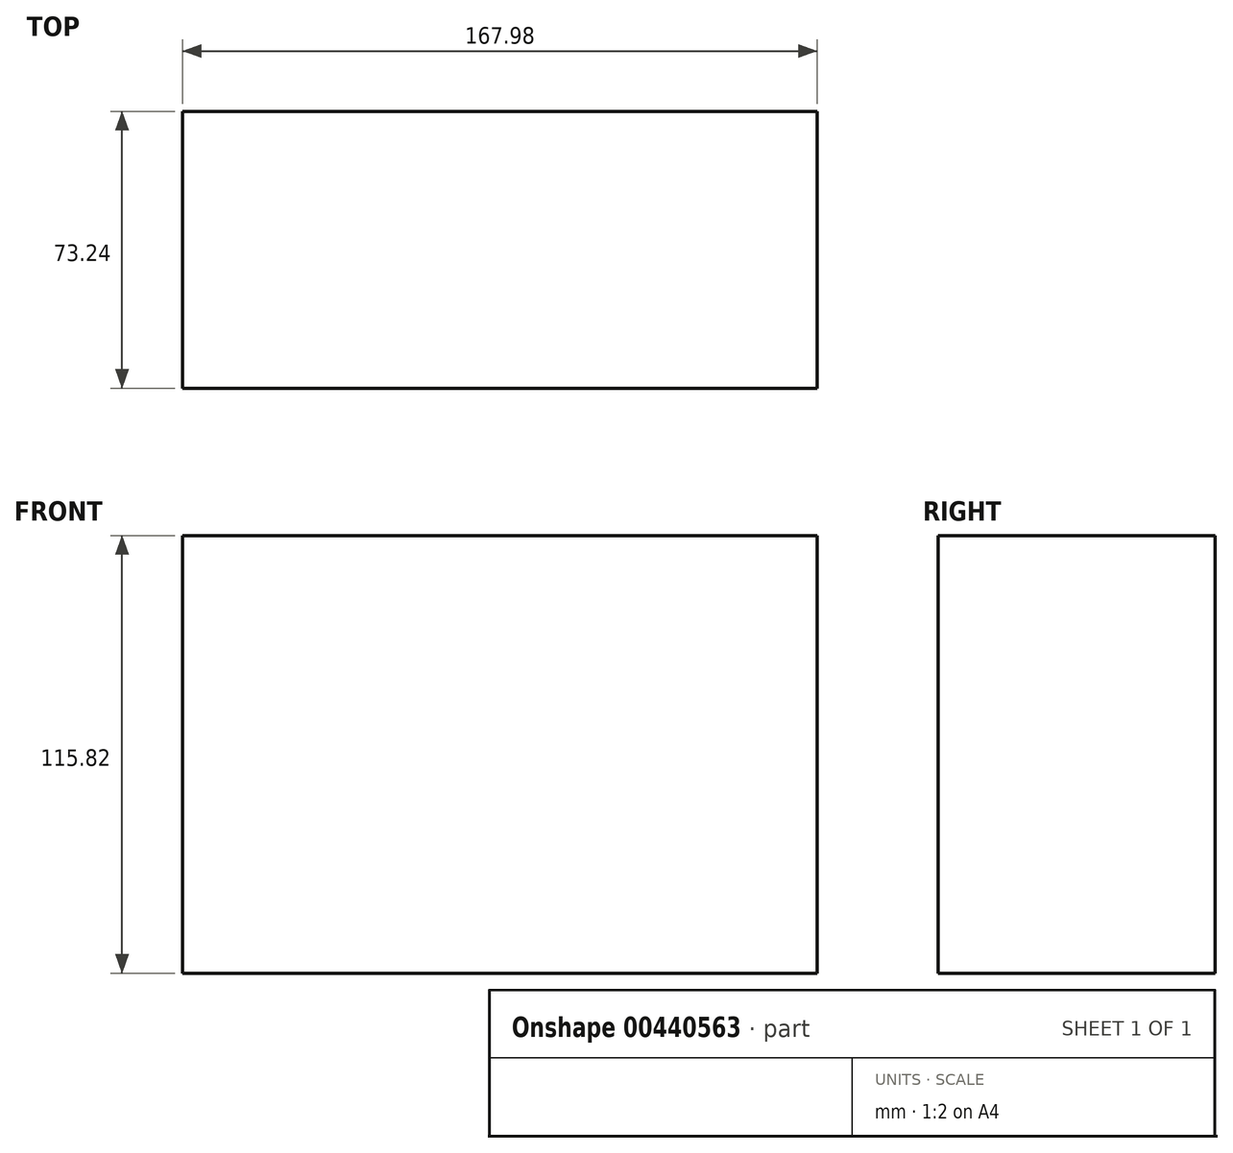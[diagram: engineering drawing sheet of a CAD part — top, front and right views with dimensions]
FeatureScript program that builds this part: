
annotation { "Feature Type Name" : "Feature", "Feature Type Description" : "" }
export const myFeature = defineFeature(function(context is Context, id is Id, definition is map)
    precondition{}
    {
        {
            var Q0;
            Q0=qCreatedBy(makeId("Top.planeOp"),FACE);
            var sketch = newSketch(context, id + "F0", { "sketchPlane" : qUnion([Q0])});
            skLineSegment(sketch, "E0.bottom", {"start": v(-116.43, 35.85) * mm, "end": v(51.55, 35.85) * mm});
            skLineSegment(sketch, "E0.top", {"start": v(-116.43, -37.39) * mm, "end": v(51.55, -37.39) * mm});
            skLineSegment(sketch, "E0.left", {"start": v(-116.43, 35.85) * mm, "end": v(-116.43, -37.39) * mm});
            skLineSegment(sketch, "E0.right", {"start": v(51.55, 35.85) * mm, "end": v(51.55, -37.39) * mm});
            skSolve(sketch);
        }
        {
            var Q0;
            Q0=makeQuery(id+"F0.imprint","IMPRINT",FACE,{"disambiguationData":[TD([[makeQuery(id+"F0.imprint","IMPRINT",EDGE,{"derivedFrom":sQuery(id+"F0.wireOp",EDGE,"E0.bottom")}),-1.0]])]});
            extrude(context, id + "F1", {"entities" : qUnion([Q0]), "flatOperationType" : FlatOperationType.REMOVE, "offsetDistance" : 25.4 * mm, "depth" : 115.82 * mm, "domain" : OperationDomain.MODEL});
        }
    });
